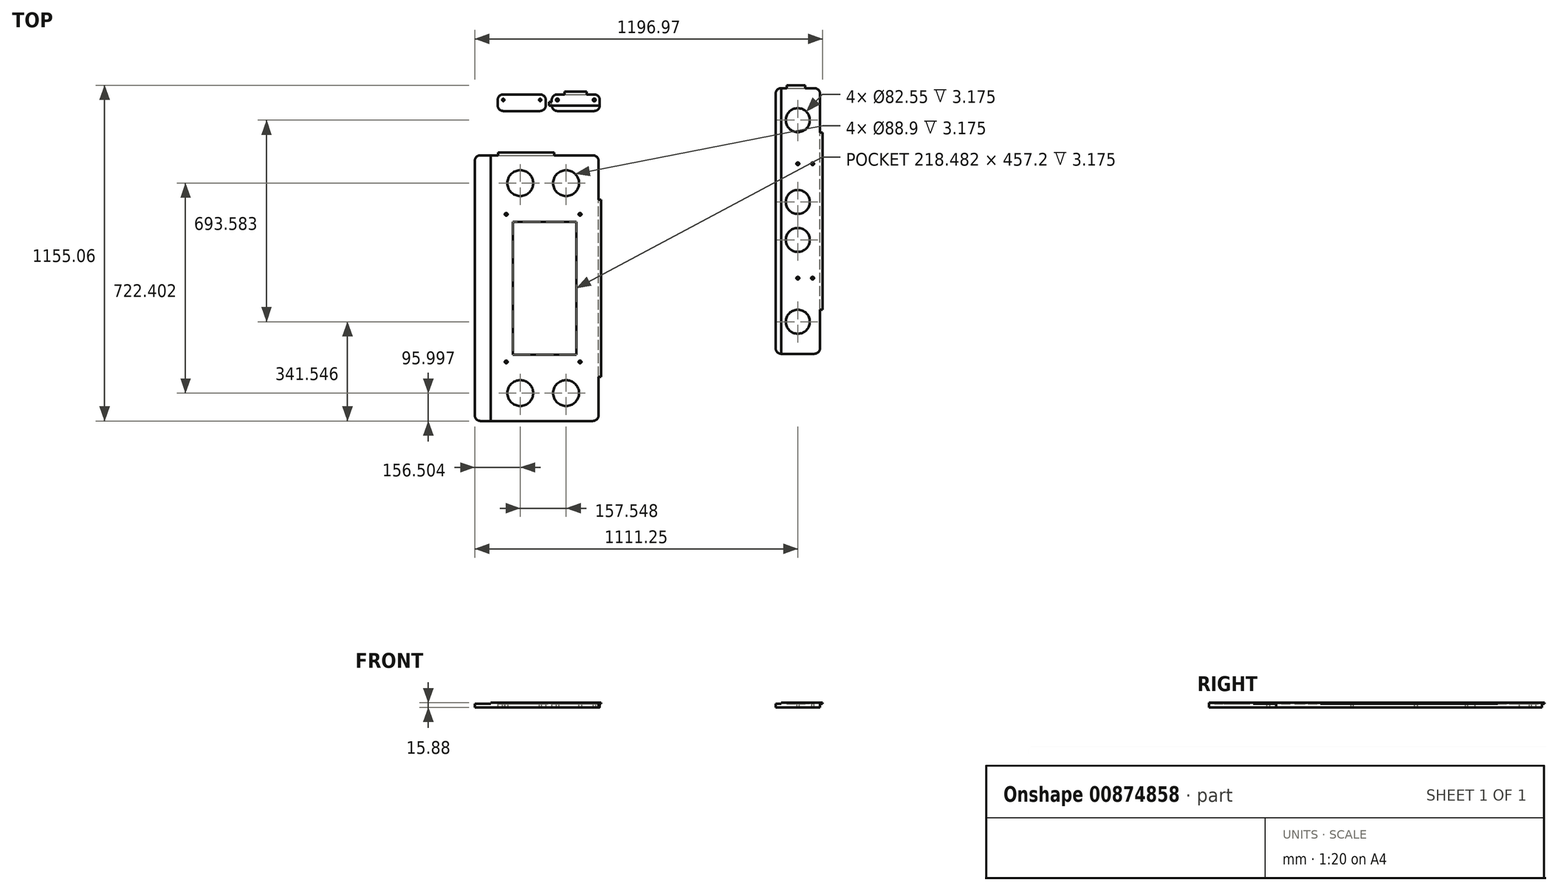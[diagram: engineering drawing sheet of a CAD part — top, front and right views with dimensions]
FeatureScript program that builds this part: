
annotation { "Feature Type Name" : "Feature", "Feature Type Description" : "" }
export const myFeature = defineFeature(function(context is Context, id is Id, definition is map)
    precondition{}
    {
        {
            var Q0;
            Q0=qCreatedBy(makeId("Top.planeOp"),FACE);
            var sketch = newSketch(context, id + "F0", { "sketchPlane" : qUnion([Q0])});
            skLineSegment(sketch, "E0.bottom", {"start": v(-381.47, -699.44) * mm, "end": v(5.88, -699.44) * mm});
            skLineSegment(sketch, "E0.top", {"start": v(-381.47, 214.96) * mm, "end": v(5.88, 214.96) * mm});
            skLineSegment(sketch, "E0.left", {"start": v(-400.52, -680.4) * mm, "end": v(-400.52, 195.9) * mm});
            skLineSegment(sketch, "E0.right", {"start": v(24.93, -680.4) * mm, "end": v(24.93, 195.9) * mm});
            skPoint(sketch, "E1.visualSharp", {"position": v(-400.52, 214.96) * mm});
            skArc(sketch, "E1.filletArc", {"start": v(-381.47, 214.96) * mm, "mid": v(-394.94, 209.38) * mm, "end": v(-400.52, 195.9) * mm});
            skPoint(sketch, "E2.visualSharp", {"position": v(24.93, 214.96) * mm});
            skArc(sketch, "E2.filletArc", {"start": v(24.93, 195.9) * mm, "mid": v(19.35, 209.38) * mm, "end": v(5.88, 214.96) * mm});
            skPoint(sketch, "E3.visualSharp", {"position": v(24.93, -699.44) * mm});
            skArc(sketch, "E3.filletArc", {"start": v(5.88, -699.44) * mm, "mid": v(19.35, -693.86) * mm, "end": v(24.93, -680.4) * mm});
            skPoint(sketch, "E4.visualSharp", {"position": v(-400.52, -699.44) * mm});
            skArc(sketch, "E4.filletArc", {"start": v(-400.52, -680.4) * mm, "mid": v(-394.94, -693.86) * mm, "end": v(-381.47, -699.44) * mm});
            skCircle(sketch, "E5", {"center": v(-292.57, 11.76) * mm, "radius": 4.89 * mm});
            skCircle(sketch, "E6", {"center": v(-38.57, 11.76) * mm, "radius": 4.89 * mm});
            skCircle(sketch, "E7", {"center": v(-38.57, -496.24) * mm, "radius": 4.89 * mm});
            skCircle(sketch, "E8", {"center": v(-292.57, -496.24) * mm, "radius": 4.89 * mm});
            skLineSegment(sketch, "E9.bottom", {"start": v(653.58, -468.3) * mm, "end": v(767.88, -468.3) * mm});
            skLineSegment(sketch, "E9.top", {"start": v(653.58, 446.1) * mm, "end": v(767.88, 446.1) * mm});
            skLineSegment(sketch, "E9.left", {"start": v(634.53, -449.25) * mm, "end": v(634.53, 427.05) * mm});
            skLineSegment(sketch, "E9.right", {"start": v(786.93, -449.25) * mm, "end": v(786.93, 427.05) * mm});
            skPoint(sketch, "E10.visualSharp", {"position": v(634.53, -468.3) * mm});
            skArc(sketch, "E10.filletArc", {"start": v(634.53, -449.25) * mm, "mid": v(640.1, -462.72) * mm, "end": v(653.58, -468.3) * mm});
            skPoint(sketch, "E11.visualSharp", {"position": v(786.93, -468.3) * mm});
            skArc(sketch, "E11.filletArc", {"start": v(767.88, -468.3) * mm, "mid": v(781.35, -462.72) * mm, "end": v(786.93, -449.25) * mm});
            skPoint(sketch, "E12.visualSharp", {"position": v(786.93, 446.1) * mm});
            skArc(sketch, "E12.filletArc", {"start": v(786.93, 427.05) * mm, "mid": v(781.35, 440.52) * mm, "end": v(767.88, 446.1) * mm});
            skPoint(sketch, "E13.visualSharp", {"position": v(634.53, 446.1) * mm});
            skArc(sketch, "E13.filletArc", {"start": v(653.58, 446.1) * mm, "mid": v(640.1, 440.52) * mm, "end": v(634.53, 427.05) * mm});
            skCircle(sketch, "E14", {"center": v(710.73, -207.95) * mm, "radius": 3.98 * mm});
            skCircle(sketch, "E15", {"center": v(761.53, -207.95) * mm, "radius": 3.98 * mm});
            skCircle(sketch, "E16", {"center": v(761.53, 185.75) * mm, "radius": 3.98 * mm});
            skCircle(sketch, "E17", {"center": v(710.73, 185.75) * mm, "radius": 3.98 * mm});
            skLineSegment(sketch, "E18.bottom", {"start": v(-302.73, 367.36) * mm, "end": v(-175.73, 367.36) * mm});
            skLineSegment(sketch, "E18.top", {"start": v(-302.73, 424.5) * mm, "end": v(-175.73, 424.5) * mm});
            skLineSegment(sketch, "E18.left", {"start": v(-321.78, 386.4) * mm, "end": v(-321.78, 405.46) * mm});
            skLineSegment(sketch, "E18.right", {"start": v(-156.68, 386.4) * mm, "end": v(-156.68, 405.46) * mm});
            skPoint(sketch, "E19.visualSharp", {"position": v(-321.78, 424.5) * mm});
            skArc(sketch, "E19.filletArc", {"start": v(-302.73, 424.5) * mm, "mid": v(-316.2, 418.93) * mm, "end": v(-321.78, 405.46) * mm});
            skPoint(sketch, "E20.visualSharp", {"position": v(-400.52, 227.66) * mm});
            skArc(sketch, "E20.filletArc", {"start": v(-321.78, 386.4) * mm, "mid": v(-316.2, 372.94) * mm, "end": v(-302.73, 367.36) * mm});
            skPoint(sketch, "E21.visualSharp", {"position": v(-235.42, 227.66) * mm});
            skArc(sketch, "E21.filletArc", {"start": v(-175.73, 367.36) * mm, "mid": v(-162.26, 372.94) * mm, "end": v(-156.68, 386.4) * mm});
            skPoint(sketch, "E22.visualSharp", {"position": v(-156.68, 424.5) * mm});
            skArc(sketch, "E22.filletArc", {"start": v(-156.68, 405.46) * mm, "mid": v(-162.26, 418.93) * mm, "end": v(-175.73, 424.5) * mm});
            skCircle(sketch, "E23", {"center": v(-302.73, 405.46) * mm, "radius": 3.98 * mm});
            skCircle(sketch, "E24", {"center": v(-175.73, 405.46) * mm, "radius": 3.98 * mm});
            skArc(sketch, "E25.1.0.0", {"start": v(-116.8, 424.5) * mm, "mid": v(-130.27, 418.93) * mm, "end": v(-135.85, 405.46) * mm});
            skArc(sketch, "E25.1.0.1", {"start": v(29.25, 405.46) * mm, "mid": v(23.67, 418.93) * mm, "end": v(10.2, 424.5) * mm});
            skPoint(sketch, "E25.1.0.2", {"position": v(-214.6, 227.66) * mm});
            skArc(sketch, "E25.1.0.3", {"start": v(-135.85, 386.4) * mm, "mid": v(-130.27, 372.94) * mm, "end": v(-116.8, 367.36) * mm});
            skLineSegment(sketch, "E25.1.0.4", {"start": v(-116.8, 367.36) * mm, "end": v(10.2, 367.36) * mm});
            skPoint(sketch, "E25.1.0.5", {"position": v(-214.6, 214.96) * mm});
            skPoint(sketch, "E25.1.0.6", {"position": v(-49.5, 227.66) * mm});
            skPoint(sketch, "E25.1.0.7", {"position": v(-135.85, 424.5) * mm});
            skLineSegment(sketch, "E25.1.0.8", {"start": v(-116.8, 424.5) * mm, "end": v(10.2, 424.5) * mm});
            skArc(sketch, "E25.1.0.9", {"start": v(10.2, 367.36) * mm, "mid": v(23.67, 372.94) * mm, "end": v(29.25, 386.4) * mm});
            skPoint(sketch, "E25.1.0.10", {"position": v(29.25, 424.5) * mm});
            skCircle(sketch, "E25.1.0.11", {"center": v(-116.8, 405.46) * mm, "radius": 3.98 * mm});
            skCircle(sketch, "E25.1.0.12", {"center": v(10.2, 405.46) * mm, "radius": 3.98 * mm});
            skLineSegment(sketch, "E25.1.0.13", {"start": v(-135.85, 386.4) * mm, "end": v(-135.85, 405.46) * mm});
            skLineSegment(sketch, "E25.1.0.14", {"start": v(29.25, 386.4) * mm, "end": v(29.25, 405.46) * mm});
            skLineSegment(sketch, "E25.direction1", {"start": v(-400.52, 214.96) * mm, "end": v(-214.6, 214.96) * mm, "construction": true});
            skSolve(sketch);
        }
        {
            var Q0;
            Q0 = qSketchRegion(id + "F0", true);
            extrude(context, id + "F1", {"entities" : qUnion([Q0]), "depth" : 12.7 * mm, "offsetDistance" : 25.4 * mm});
        }
        {
            var Q0;
            Q0=makeQuery(id+"F1.opExtrude","CAP_FACE",FACE,{"disambiguationData":[OSD([sQuery(id+"F0.wireOp",EDGE,"E0.bottom"),sQuery(id+"F0.wireOp",EDGE,"E0.top"),sQuery(id+"F0.wireOp",EDGE,"E0.left"),sQuery(id+"F0.wireOp",EDGE,"E0.right"),sQuery(id+"F0.wireOp",EDGE,"E1.filletArc"),sQuery(id+"F0.wireOp",EDGE,"E2.filletArc"),sQuery(id+"F0.wireOp",EDGE,"E3.filletArc"),sQuery(id+"F0.wireOp",EDGE,"E4.filletArc"),sQuery(id+"F0.wireOp",EDGE,"E5"),sQuery(id+"F0.wireOp",EDGE,"E6"),sQuery(id+"F0.wireOp",EDGE,"E7"),sQuery(id+"F0.wireOp",EDGE,"E8")])],"isStart":false});
            var sketch = newSketch(context, id + "F2", { "sketchPlane" : qUnion([Q0])});
            skLineSegment(sketch, "E26.bottom", {"start": v(-345.95, -699.44) * mm, "end": v(5.88, -699.44) * mm});
            skLineSegment(sketch, "E26.top", {"start": v(-345.95, 214.96) * mm, "end": v(-320.55, 214.96) * mm});
            skLineSegment(sketch, "E26.left", {"start": v(-345.95, -699.44) * mm, "end": v(-345.95, 214.96) * mm});
            skLineSegment(sketch, "E26.right", {"start": v(24.93, -680.4) * mm, "end": v(24.93, -547.04) * mm});
            skPoint(sketch, "E27.visualSharp", {"position": v(24.93, 214.96) * mm});
            skArc(sketch, "E27.filletArc", {"start": v(24.93, 195.9) * mm, "mid": v(19.35, 209.38) * mm, "end": v(5.88, 214.96) * mm});
            skPoint(sketch, "E28.visualSharp", {"position": v(24.93, -699.44) * mm});
            skArc(sketch, "E28.filletArc", {"start": v(5.88, -699.44) * mm, "mid": v(19.35, -693.86) * mm, "end": v(24.93, -680.4) * mm});
            skLineSegment(sketch, "E29.top", {"start": v(-320.55, 224.48) * mm, "end": v(-127.47, 224.48) * mm});
            skLineSegment(sketch, "E29.left", {"start": v(-320.55, 214.96) * mm, "end": v(-320.55, 224.48) * mm});
            skLineSegment(sketch, "E29.right", {"start": v(-127.47, 214.96) * mm, "end": v(-127.47, 224.48) * mm});
            skLineSegment(sketch, "E30.bottom", {"start": v(24.93, -547.04) * mm, "end": v(34.45, -547.04) * mm});
            skLineSegment(sketch, "E30.top", {"start": v(24.93, 62.56) * mm, "end": v(34.45, 62.56) * mm});
            skLineSegment(sketch, "E30.right", {"start": v(34.45, -547.04) * mm, "end": v(34.45, 62.56) * mm});
            skLineSegment(sketch, "E31.trimOffspring", {"start": v(-127.47, 214.96) * mm, "end": v(5.88, 214.96) * mm});
            skLineSegment(sketch, "E32.trimOffspring", {"start": v(24.93, 62.56) * mm, "end": v(24.93, 195.9) * mm});
            skLineSegment(sketch, "E33.bottom", {"start": v(-269.75, -470.84) * mm, "end": v(-51.27, -470.84) * mm});
            skLineSegment(sketch, "E33.top", {"start": v(-269.75, -13.64) * mm, "end": v(-51.27, -13.64) * mm});
            skLineSegment(sketch, "E33.left", {"start": v(-269.75, -470.84) * mm, "end": v(-269.75, -13.64) * mm});
            skLineSegment(sketch, "E33.right", {"start": v(-51.27, -470.84) * mm, "end": v(-51.27, -13.64) * mm});
            skCircle(sketch, "E34", {"center": v(-244.02, 118.96) * mm, "radius": 44.45 * mm});
            skCircle(sketch, "E35", {"center": v(-86.47, 118.96) * mm, "radius": 44.45 * mm});
            skCircle(sketch, "E36.MirrorC", {"center": v(-86.47, -603.44) * mm, "radius": 44.45 * mm});
            skCircle(sketch, "E37.MirrorC", {"center": v(-244.02, -603.44) * mm, "radius": 44.45 * mm});
            skCircle(sketch, "E38", {"center": v(-292.57, 11.76) * mm, "radius": 4.89 * mm});
            skCircle(sketch, "E39", {"center": v(-38.57, 11.76) * mm, "radius": 4.89 * mm});
            skCircle(sketch, "E40", {"center": v(-38.57, -496.24) * mm, "radius": 4.89 * mm});
            skCircle(sketch, "E41", {"center": v(-292.57, -496.24) * mm, "radius": 4.89 * mm});
            skSolve(sketch);
        }
        {
            var Q0;
            Q0 = qSketchRegion(id + "F2", true);
            extrude(context, id + "F3", {"entities" : qUnion([Q0]), "operationType" : NewBodyOperationType.ADD, "depth" : 3.17 * mm, "offsetDistance" : 25.4 * mm});
        }
        {
            var Q0;
            Q0=makeQuery(id+"F1.opExtrude","CAP_FACE",FACE,{"disambiguationData":[OSD([sQuery(id+"F0.wireOp",EDGE,"E9.bottom"),sQuery(id+"F0.wireOp",EDGE,"E9.top"),sQuery(id+"F0.wireOp",EDGE,"E9.left"),sQuery(id+"F0.wireOp",EDGE,"E9.right"),sQuery(id+"F0.wireOp",EDGE,"E10.filletArc"),sQuery(id+"F0.wireOp",EDGE,"E11.filletArc"),sQuery(id+"F0.wireOp",EDGE,"E12.filletArc"),sQuery(id+"F0.wireOp",EDGE,"E13.filletArc"),sQuery(id+"F0.wireOp",EDGE,"E14"),sQuery(id+"F0.wireOp",EDGE,"E15"),sQuery(id+"F0.wireOp",EDGE,"E16"),sQuery(id+"F0.wireOp",EDGE,"E17")])],"isStart":false});
            var sketch = newSketch(context, id + "F4", { "sketchPlane" : qUnion([Q0])});
            skLineSegment(sketch, "E42.bottom", {"start": v(653.58, -468.3) * mm, "end": v(767.88, -468.3) * mm});
            skLineSegment(sketch, "E42.top", {"start": v(653.58, 446.1) * mm, "end": v(672.63, 446.1) * mm});
            skLineSegment(sketch, "E42.left", {"start": v(653.58, -468.3) * mm, "end": v(653.58, 446.1) * mm});
            skLineSegment(sketch, "E42.right", {"start": v(786.93, -449.25) * mm, "end": v(786.93, -315.9) * mm});
            skPoint(sketch, "E43.visualSharp", {"position": v(786.93, 446.1) * mm});
            skArc(sketch, "E43.filletArc", {"start": v(786.93, 427.05) * mm, "mid": v(781.35, 440.52) * mm, "end": v(767.88, 446.1) * mm});
            skPoint(sketch, "E44.visualSharp", {"position": v(786.93, -468.3) * mm});
            skArc(sketch, "E44.filletArc", {"start": v(767.88, -468.3) * mm, "mid": v(781.35, -462.72) * mm, "end": v(786.93, -449.25) * mm});
            skLineSegment(sketch, "E45.top", {"start": v(672.63, 455.62) * mm, "end": v(736.13, 455.62) * mm});
            skLineSegment(sketch, "E45.right", {"start": v(736.13, 446.1) * mm, "end": v(736.13, 455.62) * mm});
            skLineSegment(sketch, "E46.bottom", {"start": v(786.93, 293.7) * mm, "end": v(796.45, 293.7) * mm});
            skLineSegment(sketch, "E46.top", {"start": v(786.93, -315.9) * mm, "end": v(796.45, -315.9) * mm});
            skLineSegment(sketch, "E46.right", {"start": v(796.45, 293.7) * mm, "end": v(796.45, -315.9) * mm});
            skLineSegment(sketch, "E47", {"start": v(672.63, 455.62) * mm, "end": v(672.63, 446.1) * mm});
            skLineSegment(sketch, "E48.trimOffspring", {"start": v(736.13, 446.1) * mm, "end": v(767.88, 446.1) * mm});
            skLineSegment(sketch, "E49.trimOffspring", {"start": v(786.93, 293.7) * mm, "end": v(786.93, 427.05) * mm});
            skCircle(sketch, "E50", {"center": v(710.73, 185.75) * mm, "radius": 4.89 * mm});
            skCircle(sketch, "E51", {"center": v(761.53, 185.75) * mm, "radius": 4.89 * mm});
            skCircle(sketch, "E52", {"center": v(761.53, -207.95) * mm, "radius": 4.89 * mm});
            skCircle(sketch, "E53", {"center": v(710.73, -207.95) * mm, "radius": 4.89 * mm});
            skCircle(sketch, "E54", {"center": v(710.73, -357.9) * mm, "radius": 41.28 * mm});
            skPoint(sketch, "E54.centerSnap0", {"position": v(710.73, -468.3) * mm});
            skCircle(sketch, "E55", {"center": v(710.73, -76.37) * mm, "radius": 41.28 * mm});
            skCircle(sketch, "E56.MirrorC", {"center": v(710.73, 335.69) * mm, "radius": 41.28 * mm});
            skCircle(sketch, "E57.MirrorC", {"center": v(710.73, 54.17) * mm, "radius": 41.28 * mm});
            skSolve(sketch);
        }
        {
            var Q0;
            Q0 = qSketchRegion(id + "F4", true);
            extrude(context, id + "F5", {"entities" : qUnion([Q0]), "operationType" : NewBodyOperationType.ADD, "depth" : 3.17 * mm, "offsetDistance" : 25.4 * mm});
        }
        {
            var Q0;
            Q0=makeQuery(id+"F1.opExtrude","CAP_FACE",FACE,{"disambiguationData":[OSD([sQuery(id+"F0.wireOp",EDGE,"E25.1.0.0"),sQuery(id+"F0.wireOp",EDGE,"E25.1.0.1"),sQuery(id+"F0.wireOp",EDGE,"E25.1.0.3"),sQuery(id+"F0.wireOp",EDGE,"E25.1.0.4"),sQuery(id+"F0.wireOp",EDGE,"E25.1.0.8"),sQuery(id+"F0.wireOp",EDGE,"E25.1.0.9"),sQuery(id+"F0.wireOp",EDGE,"E25.1.0.11"),sQuery(id+"F0.wireOp",EDGE,"E25.1.0.12"),sQuery(id+"F0.wireOp",EDGE,"E25.1.0.13"),sQuery(id+"F0.wireOp",EDGE,"E25.1.0.14")])],"isStart":false});
            var sketch = newSketch(context, id + "F6", { "sketchPlane" : qUnion([Q0])});
            skLineSegment(sketch, "E58.bottom", {"start": v(-135.85, 386.4) * mm, "end": v(29.25, 386.4) * mm});
            skLineSegment(sketch, "E58.top", {"start": v(-116.8, 424.5) * mm, "end": v(-91.4, 424.5) * mm});
            skLineSegment(sketch, "E58.left", {"start": v(-135.85, 399.1) * mm, "end": v(-135.85, 405.46) * mm});
            skLineSegment(sketch, "E58.right", {"start": v(29.25, 386.4) * mm, "end": v(29.25, 405.46) * mm});
            skPoint(sketch, "E59.visualSharp", {"position": v(-135.85, 424.5) * mm});
            skArc(sketch, "E59.filletArc", {"start": v(-116.8, 424.5) * mm, "mid": v(-130.27, 418.93) * mm, "end": v(-135.85, 405.46) * mm});
            skPoint(sketch, "E60.visualSharp", {"position": v(29.25, 424.5) * mm});
            skArc(sketch, "E60.filletArc", {"start": v(29.25, 405.46) * mm, "mid": v(23.67, 418.93) * mm, "end": v(10.2, 424.5) * mm});
            skLineSegment(sketch, "E61.top", {"start": v(-91.4, 434.03) * mm, "end": v(-15.2, 434.03) * mm});
            skLineSegment(sketch, "E61.left", {"start": v(-91.4, 424.5) * mm, "end": v(-91.4, 434.03) * mm});
            skLineSegment(sketch, "E61.right", {"start": v(-15.2, 424.5) * mm, "end": v(-15.2, 434.03) * mm});
            skLineSegment(sketch, "E62.bottom", {"start": v(-135.85, 386.4) * mm, "end": v(-145.38, 386.4) * mm});
            skLineSegment(sketch, "E62.top", {"start": v(-135.85, 399.1) * mm, "end": v(-145.38, 399.1) * mm});
            skLineSegment(sketch, "E62.right", {"start": v(-145.38, 386.4) * mm, "end": v(-145.38, 399.1) * mm});
            skCircle(sketch, "E63", {"center": v(-116.8, 405.46) * mm, "radius": 4.89 * mm});
            skCircle(sketch, "E64", {"center": v(10.2, 405.46) * mm, "radius": 4.89 * mm});
            skLineSegment(sketch, "E65.trimOffspring", {"start": v(-15.2, 424.5) * mm, "end": v(10.2, 424.5) * mm});
            skSolve(sketch);
        }
        {
            var Q0;
            Q0 = qSketchRegion(id + "F6", true);
            extrude(context, id + "F7", {"entities" : qUnion([Q0]), "operationType" : NewBodyOperationType.ADD, "depth" : 3.17 * mm, "offsetDistance" : 25.4 * mm});
        }
    });
